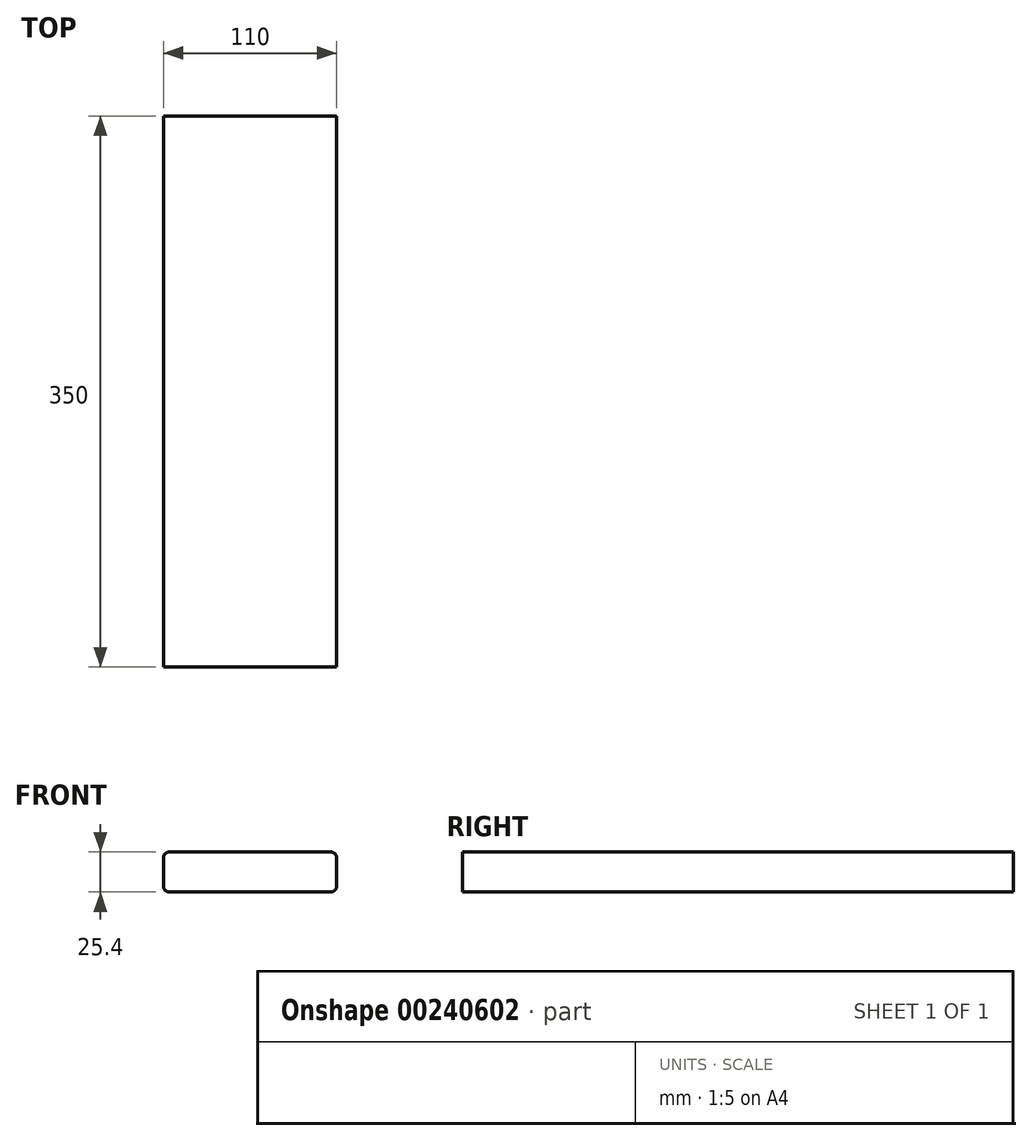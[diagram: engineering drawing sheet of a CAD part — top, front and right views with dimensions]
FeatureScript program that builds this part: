
annotation { "Feature Type Name" : "Feature", "Feature Type Description" : "" }
export const myFeature = defineFeature(function(context is Context, id is Id, definition is map)
    precondition{}
    {
        {
            var Q0;
            Q0=qCreatedBy(makeId("Top.planeOp"),FACE);
            var sketch = newSketch(context, id + "F0", { "sketchPlane" : qUnion([Q0])});
            skLineSegment(sketch, "E0.bottom", {"start": v(55, 175) * mm, "end": v(-55, 175) * mm});
            skLineSegment(sketch, "E0.top", {"start": v(55, -175) * mm, "end": v(-55, -175) * mm});
            skLineSegment(sketch, "E0.left", {"start": v(55, 175) * mm, "end": v(55, -175) * mm});
            skLineSegment(sketch, "E0.right", {"start": v(-55, 175) * mm, "end": v(-55, -175) * mm});
            skPoint(sketch, "E0.middle", {"position": v(0, 0) * mm});
            skSolve(sketch);
        }
        {
            var Q0;
            Q0=makeQuery(id+"F0.imprint","IMPRINT",FACE,{"disambiguationData":[TD([[makeQuery(id+"F0.imprint","IMPRINT",EDGE,{"derivedFrom":sQuery(id+"F0.wireOp",EDGE,"E0.bottom")}),1.0]])]});
            extrude(context, id + "F1", {"entities" : qUnion([Q0]), "endBound" : BoundingType.SYMMETRIC, "depth" : 25.4 * mm});
        }
        {
            var Q0;
            Q0=makeQuery(id+"F1.opExtrude","CAP_EDGE",EDGE,{"disambiguationData":[OSD([sQuery(id+"F0.wireOp",EDGE,"E0.left")])],"isStart":false});
            var Q1;
            Q1=makeQuery(id+"F1.opExtrude","CAP_EDGE",EDGE,{"disambiguationData":[OSD([sQuery(id+"F0.wireOp",EDGE,"E0.left")])],"isStart":true});
            var Q2;
            Q2=makeQuery(id+"F1.opExtrude","CAP_EDGE",EDGE,{"disambiguationData":[OSD([sQuery(id+"F0.wireOp",EDGE,"E0.right")])],"isStart":false});
            var Q3;
            Q3=makeQuery(id+"F1.opExtrude","CAP_EDGE",EDGE,{"disambiguationData":[OSD([sQuery(id+"F0.wireOp",EDGE,"E0.right")])],"isStart":true});
            fillet(context, id + "F2", {"entities" : qUnion([Q0, Q1, Q2, Q3]), "radius" : 3.8 * mm, "tangentPropagation" : true, "allowEdgeOverflow" : false});
        }
    });
